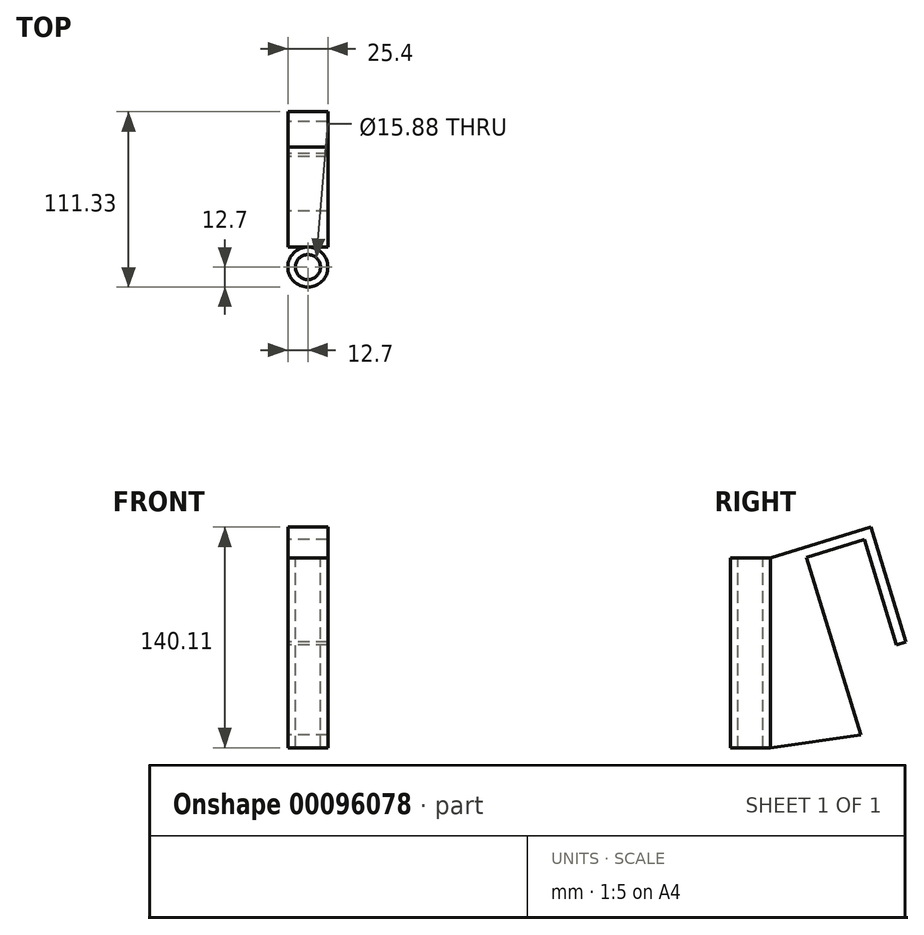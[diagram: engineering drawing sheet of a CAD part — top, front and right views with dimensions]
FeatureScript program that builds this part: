
annotation { "Feature Type Name" : "Feature", "Feature Type Description" : "" }
export const myFeature = defineFeature(function(context is Context, id is Id, definition is map)
    precondition{}
    {
        {
            var Q0;
            Q0=qCreatedBy(makeId("Right.planeOp"),FACE);
            var sketch = newSketch(context, id + "F0", { "sketchPlane" : qUnion([Q0])});
            skLineSegment(sketch, "E0", {"start": v(50.8, 0) * mm, "end": v(97.68, -152.4) * mm});
            skLineSegment(sketch, "E1", {"start": v(97.68, -152.4) * mm, "end": v(0, -152.4) * mm});
            skLineSegment(sketch, "E2", {"start": v(0, -152.4) * mm, "end": v(0, 0) * mm});
            skLineSegment(sketch, "E3", {"start": v(0, 0) * mm, "end": v(50.8, 0) * mm});
            skLineSegment(sketch, "E4", {"start": v(50.8, 0) * mm, "end": v(99.35, 14.94) * mm});
            skLineSegment(sketch, "E5", {"start": v(99.35, 14.94) * mm, "end": v(136.7, -106.45) * mm});
            skLineSegment(sketch, "E6", {"start": v(136.7, -106.45) * mm, "end": v(185.25, -91.51) * mm});
            skLineSegment(sketch, "E7", {"start": v(185.25, -91.51) * mm, "end": v(165.74, -28.1) * mm});
            skLineSegment(sketch, "E8", {"start": v(165.74, -28.1) * mm, "end": v(113.48, 57.58) * mm});
            skLineSegment(sketch, "E9", {"start": v(113.48, 57.58) * mm, "end": v(40.6, 31.34) * mm});
            skLineSegment(sketch, "E10", {"start": v(40.6, 31.34) * mm, "end": v(50.8, 0) * mm});
            skLineSegment(sketch, "E11", {"start": v(40.6, 31.34) * mm, "end": v(0, 0) * mm});
            skSolve(sketch);
        }
        {
            var Q0;
            Q0=qCreatedBy(makeId("Top.planeOp"),FACE);
            var sketch = newSketch(context, id + "F1", { "sketchPlane" : qUnion([Q0])});
            skCircle(sketch, "E12", {"center": v(0, -12.7) * mm, "radius": 12.7 * mm});
            skCircle(sketch, "E13", {"center": v(0, -12.7) * mm, "radius": 7.94 * mm});
            skSolve(sketch);
        }
        {
            var Q0;
            Q0=makeQuery(id+"F1.imprint","IMPRINT",FACE,{"disambiguationData":[TD([[makeQuery(id+"F1.imprint","IMPRINT",EDGE,{"derivedFrom":sQuery(id+"F1.wireOp",EDGE,"E12")}),1.0]])]});
            extrude(context, id + "F2", {"entities" : qUnion([Q0]), "oppositeDirection" : true, "depth" : 120.65 * mm});
        }
        {
            var Q0;
            Q0=makeQuery(id+"F0.imprint","IMPRINT",FACE,{"disambiguationData":[TD([[makeQuery(id+"F0.imprint","IMPRINT",EDGE,{"derivedFrom":sQuery(id+"F0.wireOp",EDGE,"E0")}),-1.0]])]});
            var Q1;
            Q1=makeQuery(id+"F0.imprint","IMPRINT",FACE,{"disambiguationData":[TD([[makeQuery(id+"F0.imprint","IMPRINT",EDGE,{"derivedFrom":sQuery(id+"F0.wireOp",EDGE,"E3")}),1.0]])]});
            var Q2;
            Q2=makeQuery(id+"F0.imprint","IMPRINT",FACE,{"disambiguationData":[TD([[makeQuery(id+"F0.imprint","IMPRINT",EDGE,{"derivedFrom":sQuery(id+"F0.wireOp",EDGE,"E4")}),1.0]])]});
            extrude(context, id + "F3", {"entities" : qUnion([Q0, Q1, Q2]), "operationType" : NewBodyOperationType.ADD, "endBound" : BoundingType.SYMMETRIC, "depth" : 25.4 * mm});
        }
        {
            var Q0;
            Q0=makeQuery(id+"F3.opExtrude","SWEPT_BODY",BODY,{"disambiguationData":[OSD([sQuery(id+"F0.wireOp",EDGE,"E0"),sQuery(id+"F0.wireOp",EDGE,"E1"),sQuery(id+"F0.wireOp",EDGE,"E2"),sQuery(id+"F0.wireOp",EDGE,"E4"),sQuery(id+"F0.wireOp",EDGE,"E5"),sQuery(id+"F0.wireOp",EDGE,"E6"),sQuery(id+"F0.wireOp",EDGE,"E7"),sQuery(id+"F0.wireOp",EDGE,"E8"),sQuery(id+"F0.wireOp",EDGE,"E9"),sQuery(id+"F0.wireOp",EDGE,"E11")])]});
            deleteBodies(context, id + "F4", {"entities" : qUnion([Q0])});
        }
        {
            var Q0;
            Q0=qCreatedBy(makeId("Right.planeOp"),FACE);
            var sketch = newSketch(context, id + "F5", { "sketchPlane" : qUnion([Q0])});
            skLineSegment(sketch, "E14", {"start": v(0, 0) * mm, "end": v(63.65, 19.46) * mm});
            skLineSegment(sketch, "E15", {"start": v(63.65, 19.46) * mm, "end": v(85.93, -53.4) * mm});
            skLineSegment(sketch, "E16", {"start": v(85.93, -53.4) * mm, "end": v(79.86, -55.27) * mm});
            skLineSegment(sketch, "E17", {"start": v(79.86, -55.27) * mm, "end": v(59.44, 11.53) * mm});
            skLineSegment(sketch, "E18", {"start": v(59.44, 11.53) * mm, "end": v(22.84, 0.34) * mm});
            skLineSegment(sketch, "E19", {"start": v(22.84, 0.34) * mm, "end": v(57.36, -112.59) * mm});
            skLineSegment(sketch, "E20", {"start": v(57.36, -112.59) * mm, "end": v(0, -120.65) * mm});
            skLineSegment(sketch, "E21", {"start": v(0, 0) * mm, "end": v(0, -152.4) * mm});
            skLineSegment(sketch, "E22", {"start": v(-25.4, -152.4) * mm, "end": v(-25.4, 0) * mm});
            skSolve(sketch);
        }
        {
            var Q0;
            Q0=makeQuery(id+"F5.imprint","IMPRINT",FACE,{"disambiguationData":[TD([[makeQuery(id+"F5.imprint","IMPRINT",EDGE,{"derivedFrom":sQuery(id+"F5.wireOp",EDGE,"E14")}),-1.0]])]});
            extrude(context, id + "F6", {"entities" : qUnion([Q0]), "operationType" : NewBodyOperationType.ADD, "endBound" : BoundingType.SYMMETRIC, "depth" : 25.4 * mm});
        }
    });
